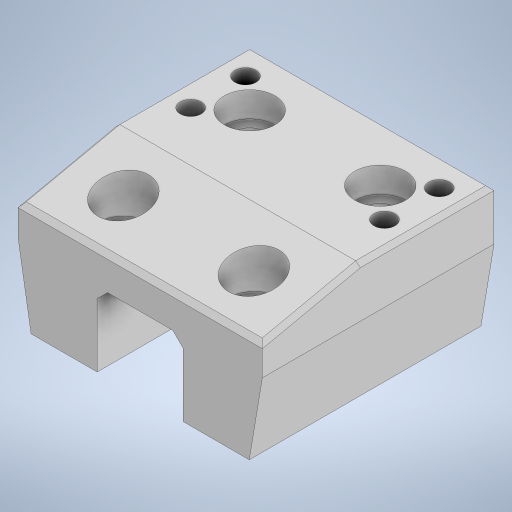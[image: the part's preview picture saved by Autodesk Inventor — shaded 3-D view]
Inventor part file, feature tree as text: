
AUTODESK INVENTOR PART (.ipt)
format: ipt  version: 2023 (Build 270158000, 158)  size: 462,848 bytes
history: native  units: in
note: dims shown in document units (in); Inventor stores cm internally (conversion verified against a paired STEP export)
features: extrude x11, sketch x7, projected_geometry x3, chamfer x2, thicken_offset x1
ambient origin geometry x8: Origin, YZ Plane, XZ Plane, XY Plane, X Axis, Y Axis, Z Axis, Center Point
bodies: Solid1 (feature_tree)
feature tree (24):
  extrude  "Extrusion1"  Depth=2.3622in
  extrude  "Extrusion2"  Depth=0.0197in
  extrude  "Extrusion3"  Depth=0.0197in
  extrude  "Extrusion4"  Depth=0.1969in
  extrude  "Extrusion5"  Depth=2.7874in
  extrude  "Extrusion6"  Depth=2.1654in TaperAngle=0.0deg
  extrude  "Extrusion9"  Depth=0.3937in TaperAngle=0.0deg
  extrude  "Extrusion10"  Depth=0.3937in TaperAngle=0.0deg
  extrude  "Extrusion11"  Depth=0.1969in
  extrude  "Extrusion12"  Depth=0.1969in TaperAngle=0.0deg
  extrude  "Extrusion13"  Depth=0.1969in
  chamfer  "Chamfer2"  Distance=0.2362in
  thicken_offset  "Thicken1"
  chamfer  "Chamfer1"  Distance=1.3937in
  sketch  "Sketch4"  dims[d0=0.9843in d1=2.3622in]
  sketch  "Sketch5"  dims[d2=0.0197in d3=0.0197in]
  sketch  "Sketch8"  dims[d4=0.0197in d5=0.0197in]
  sketch  "Sketch10"  dims[d6=0.1969in d7=1.811in]
  projected_geometry  "Projected Loop1"
  sketch  "Sketch11"  dims[d8=0.5118in d9=2.7874in]
  sketch  "Sketch12"  dims[d10=2.1654in d11=1.3937in d12=0.0in]
  sketch  "Sketch13"  dims[d13=1.3937in d14=0.0in d15=0.3937in d16=0.1969in d17=0.0in d18=0.0in d19=0.3937in d20=1.1969in d21=0.0in d22=0.0in d27=0.3937in d28=0.0in d29=0.2687in d31=1.4375in d32=0.0in d34=0.4724in d35=0.2362in d36=0.0in d50=1.3937in d51=0.0394in d52=0.1181in d53=135.0deg d54=0.0787in d55=0.1358in d56=0.689in d57=0.2819in d58=0.0935in d59=0.0525in d60=0.0953in d61=0.3937in d63=0.3937in d64=0.0in d66=0.0394in d67=0.125in d68=0.374in d69=0.689in d70=90.0deg d71=90.0deg d72=0.7874in d73=0.0394in d74=0.5315in d78=1.1811in d79=1.2205in d80=0.5315in d81=0.0787in d82=0.0787in d83=45.0deg d84=0.3937in d85=0.0in d86=2.2835in d88=0.0079in d89=0.0079in d90=0.002in d91=0.3937in d92=0.0in d93=0.1969in d94=0.0in d95=0.0in d96=0.1969in d97=0.0in d98=0.0394in d99=0.0787in d100=45.0deg d101=0.4724in d102=45.0deg d103=0.0965in]
  projected_geometry  "Projected Loop2"
  projected_geometry  "Projected Loop3"
